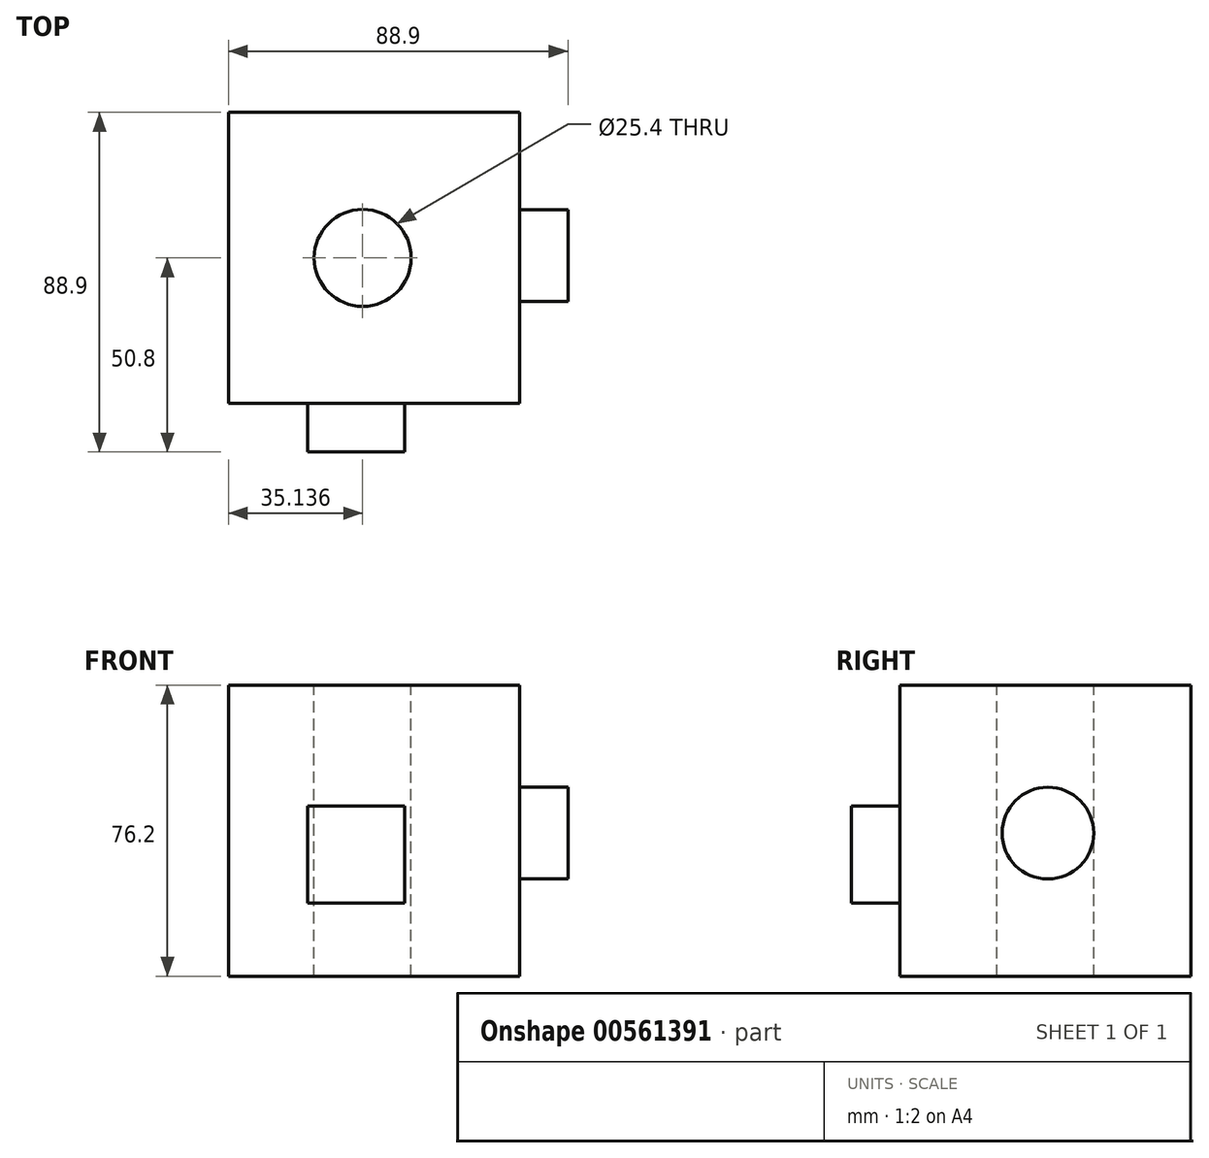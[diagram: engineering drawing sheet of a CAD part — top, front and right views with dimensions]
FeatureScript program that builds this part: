
annotation { "Feature Type Name" : "Feature", "Feature Type Description" : "" }
export const myFeature = defineFeature(function(context is Context, id is Id, definition is map)
    precondition{}
    {
        {
            var Q0;
            Q0=qCreatedBy(makeId("Front.planeOp"),FACE);
            var sketch = newSketch(context, id + "F0", { "sketchPlane" : qUnion([Q0])});
            skLineSegment(sketch, "E0.bottom", {"start": v(0, 0) * mm, "end": v(76.2, 0) * mm});
            skLineSegment(sketch, "E0.top", {"start": v(0, 76.2) * mm, "end": v(76.2, 76.2) * mm});
            skLineSegment(sketch, "E0.left", {"start": v(0, 0) * mm, "end": v(0, 76.2) * mm});
            skLineSegment(sketch, "E0.right", {"start": v(76.2, 0) * mm, "end": v(76.2, 76.2) * mm});
            skSolve(sketch);
        }
        {
            var Q0;
            Q0=makeQuery(id+"F0.imprint","IMPRINT",FACE,{"disambiguationData":[TD([[makeQuery(id+"F0.imprint","IMPRINT",EDGE,{"derivedFrom":sQuery(id+"F0.wireOp",EDGE,"E0.bottom")}),1.0]])]});
            extrude(context, id + "F1", {"entities" : qUnion([Q0]), "depth" : 76.2 * mm, "offsetDistance" : 25.4 * mm});
        }
        {
            var Q0;
            Q0=makeQuery(id+"F1.opExtrude","SWEPT_FACE",FACE,{"disambiguationData":[OSD([sQuery(id+"F0.wireOp",EDGE,"E0.top")])]});
            var sketch = newSketch(context, id + "F2", { "sketchPlane" : qUnion([Q0])});
            skPoint(sketch, "E1", {"position": v(35.14, -38.1) * mm});
            skPoint(sketch, "E1.positionSnap0", {"position": v(0, -38.1) * mm});
            skSolve(sketch);
        }
        {
            var Q0;
            Q0=sQuery(id+"F2.wireOp",VERTEX,"E1");
            var Q1;
            Q1=makeQuery(id+"F1.opExtrude","SWEPT_BODY",BODY,{"disambiguationData":[OSD([sQuery(id+"F0.wireOp",EDGE,"E0.bottom"),sQuery(id+"F0.wireOp",EDGE,"E0.top"),sQuery(id+"F0.wireOp",EDGE,"E0.left"),sQuery(id+"F0.wireOp",EDGE,"E0.right")])]});
            hole(context, id + "F3", {"style" : HoleStyle.SIMPLE, "endStyle" : HoleEndStyle.THROUGH, "holeDiameter" : 25.4 * mm, "isTappedThrough" : true, "tappedDepth" : 12.7 * mm, "tapClearance" : 3, "locations" : qUnion([Q0]), "scope" : qUnion([Q1])});
        }
        {
            var Q0;
            Q0=makeQuery(id+"F1.opExtrude","CAP_FACE",FACE,{"disambiguationData":[OSD([sQuery(id+"F0.wireOp",EDGE,"E0.bottom"),sQuery(id+"F0.wireOp",EDGE,"E0.top"),sQuery(id+"F0.wireOp",EDGE,"E0.left"),sQuery(id+"F0.wireOp",EDGE,"E0.right")])],"isStart":false});
            var sketch = newSketch(context, id + "F4", { "sketchPlane" : qUnion([Q0])});
            skPoint(sketch, "E2", {"position": v(37.1, 39.85) * mm});
            skSolve(sketch);
        }
        {
            var Q0;
            Q0=makeQuery(id+"F4.imprint","IMPRINT",FACE,{"disambiguationData":[TD([[makeQuery(id+"F4.imprint","IMPRINT",EDGE,{"derivedFrom":makeQuery(id+"F1.opExtrude","CAP_EDGE",EDGE,{"disambiguationData":[OSD([sQuery(id+"F0.wireOp",EDGE,"E0.bottom")])],"isStart":false})}),1.0]])]});
            var sketch = newSketch(context, id + "F5", { "sketchPlane" : qUnion([Q0])});
            skLineSegment(sketch, "E3.bottom", {"start": v(20.73, 44.57) * mm, "end": v(46.13, 44.57) * mm});
            skLineSegment(sketch, "E3.top", {"start": v(20.73, 19.17) * mm, "end": v(46.13, 19.17) * mm});
            skLineSegment(sketch, "E3.left", {"start": v(20.73, 44.57) * mm, "end": v(20.73, 19.17) * mm});
            skLineSegment(sketch, "E3.right", {"start": v(46.13, 44.57) * mm, "end": v(46.13, 19.17) * mm});
            skSolve(sketch);
        }
        {
            var Q0;
            Q0=makeQuery(id+"F5.imprint","IMPRINT",FACE,{"disambiguationData":[TD([[makeQuery(id+"F5.imprint","IMPRINT",EDGE,{"derivedFrom":sQuery(id+"F5.wireOp",EDGE,"E3.bottom")}),-1.0]])]});
            extrude(context, id + "F6", {"entities" : qUnion([Q0]), "operationType" : NewBodyOperationType.ADD, "depth" : 12.7 * mm, "offsetDistance" : 25.4 * mm});
        }
        {
            var Q0;
            Q0=makeQuery(id+"F1.opExtrude","SWEPT_FACE",FACE,{"disambiguationData":[OSD([sQuery(id+"F0.wireOp",EDGE,"E0.right")])]});
            var sketch = newSketch(context, id + "F7", { "sketchPlane" : qUnion([Q0])});
            skCircle(sketch, "E4", {"center": v(-37.45, 37.45) * mm, "radius": 12 * mm});
            skSolve(sketch);
        }
        {
            var Q0;
            Q0=makeQuery(id+"F7.imprint","IMPRINT",FACE,{"disambiguationData":[TD([[makeQuery(id+"F7.imprint","IMPRINT",EDGE,{"derivedFrom":sQuery(id+"F7.wireOp",EDGE,"E4")}),1.0]])]});
            extrude(context, id + "F8", {"entities" : qUnion([Q0]), "operationType" : NewBodyOperationType.ADD, "depth" : 12.7 * mm, "offsetDistance" : 25.4 * mm});
        }
    });
